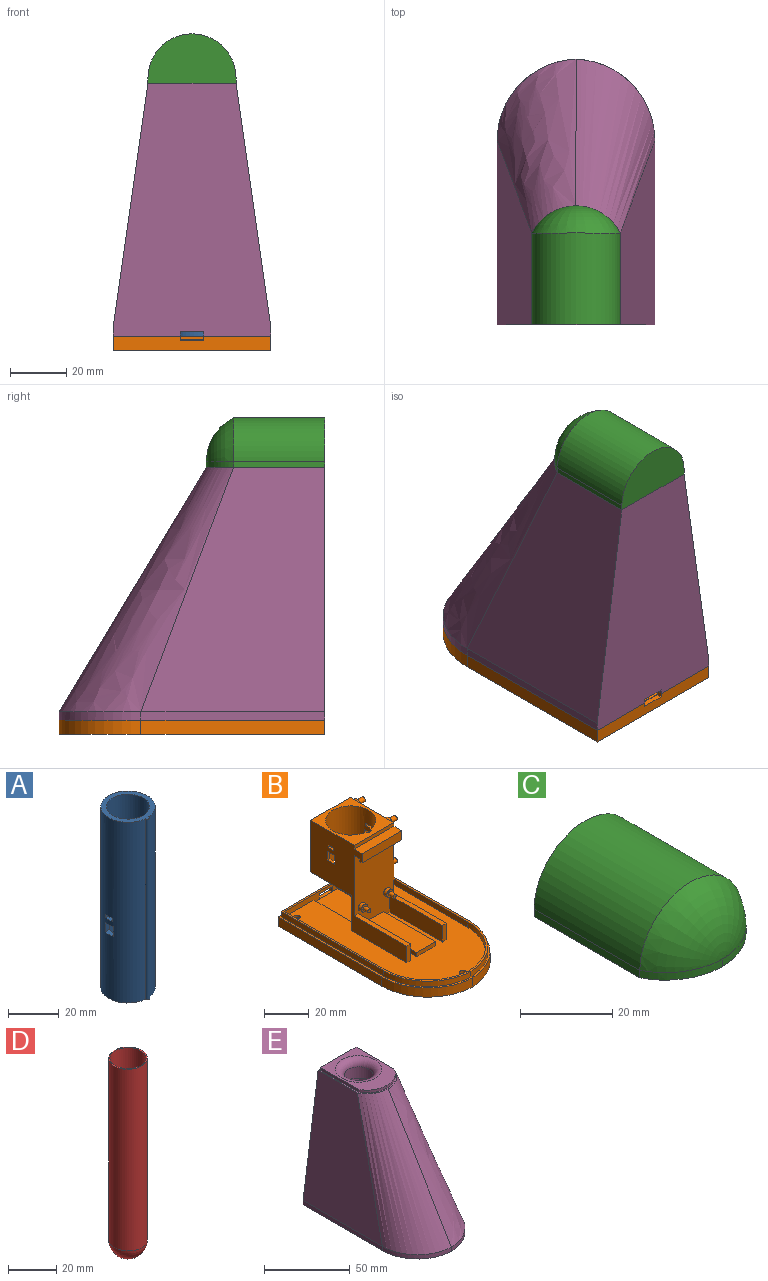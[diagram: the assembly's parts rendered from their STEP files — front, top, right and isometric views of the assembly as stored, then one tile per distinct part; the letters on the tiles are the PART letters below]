
ASSEMBLY  parts=5 mates=4
PART A: 22 faces, bbox 21.5x22.5x87.5 mm
  f0: cylinder r=8.5mm len=86.5mm, axis (0,0,1), area 4564.1mm2, adj f3,f5,f6,f7,f8,f9,f10,f11
  f1: cylinder r=10.75mm len=87.5mm, axis (0,0,1), area 5679.7mm2, adj f2,f3,f4,f6,f7,f8,f9,f10
  f2: plane 22.5x21.5mm, normal (0,0,-1), area 364.7mm2, adj f1,f4
  f3: plane 22.5x21.5mm, normal (0,0,1), area 137.7mm2, adj f0,f1,f4
  f4: cylinder r=1mm len=87.5mm, axis (0,0,1), area 283mm2, adj f1,f2,f3
  f5: plane 17x17mm, normal (0,0,1), area 227mm2, adj f0
  f6: plane 2.29x1.5mm, normal (0,-1,0), area 3.4mm2, adj f0,f1,f7,f9
  f7: plane 3.6x2.44mm, normal (0,0,1), area 8.1mm2, adj f0,f1,f6,f8
  f8: plane 2.29x1.5mm, normal (0,1,0), area 3.4mm2, adj f0,f1,f7,f9
  f9: plane 3.6x2.44mm, normal (0,0,-1), area 8.1mm2, adj f0,f1,f6,f8
  f10: plane 3.6x2.44mm, normal (0,0,-1), area 8.1mm2, adj f0,f1,f11,f13
  f11: plane 2.29x1.5mm, normal (0,1,0), area 3.4mm2, adj f0,f1,f10,f12
  f12: plane 3.6x2.44mm, normal (0,0,1), area 8.1mm2, adj f0,f1,f11,f13
  f13: plane 2.29x1.5mm, normal (0,-1,0), area 3.4mm2, adj f0,f1,f10,f12
  f14: plane 4.8x2.32mm, normal (0,1,0), area 11.1mm2, adj f0,f1,f15,f17
  f15: plane 4.6x2.57mm, normal (0,0,-1), area 10.5mm2, adj f0,f1,f14,f16
  f16: plane 4.8x2.32mm, normal (0,-1,0), area 11.1mm2, adj f0,f1,f15,f17
  f17: plane 4.6x2.57mm, normal (0,0,1), area 10.5mm2, adj f0,f1,f14,f16
  f18: plane 4.6x2.57mm, normal (0,0,1), area 10.5mm2, adj f0,f1,f19,f21
  f19: plane 4.8x2.32mm, normal (0,-1,0), area 11.1mm2, adj f0,f1,f18,f20
  f20: plane 4.6x2.57mm, normal (0,0,-1), area 10.5mm2, adj f0,f1,f19,f21
  f21: plane 4.8x2.32mm, normal (0,1,0), area 11.1mm2, adj f0,f1,f18,f20
PART B: 107 faces, bbox 56.2x94.6x52.5 mm
  f0: plane 52.2x4.2mm, normal (0,-1,0), area 151.6mm2, adj f76,f80,f82,f85,f98,f99,f101,f103
  f1: plane 54.2x3mm, normal (0,1,0), area 149.5mm2, adj f2,f79,f81,f85,f103,f104,f105
  f2: plane 94.58x56.2mm, normal (0,0,1), area 264.9mm2, adj f1,f78,f79,f81,f84,f87,f88,f89
  f3: cylinder r=1.5mm len=3mm, axis (0,0,-1), area 14.1mm2, adj f76,f97
  f4: cylinder r=1.5mm len=3mm, axis (0,0,-1), area 14.1mm2, adj f76,f95
  f5: cylinder r=1.5mm len=3mm, axis (0,0,-1), area 14.1mm2, adj f76,f93
  f6: plane 33x2.5mm, normal (0,0,1), area 82.5mm2, adj f7,f30,f38,f71
  f7: plane 9x2.5mm, normal (0,-1,0), area 22.5mm2, adj f6,f38,f71,f76
  f8: plane 12x2.21mm, normal (0,-1,0), area 26.6mm2, adj f72,f73,f74,f76
  f9: plane 4.6x1.49mm, normal (0,0,-1), area 6.1mm2, adj f16,f18,f38,f61
  f10: plane 4.8x2.49mm, normal (0,-1,0), area 11.9mm2, adj f11,f17,f60,f61
  f11: plane 4.6x2.49mm, normal (0,0,1), area 10.7mm2, adj f10,f37,f60,f61
  f12: plane 3.6x1.4mm, normal (0,0,-1), area 4.7mm2, adj f21,f35,f38,f61
  f13: plane 1.5x1.4mm, normal (0,-1,0), area 2.1mm2, adj f20,f22,f39,f61
  f14: plane 3.6x1.4mm, normal (0,0,1), area 4.7mm2, adj f21,f35,f38,f61
  f15: plane 1.5x1.4mm, normal (0,1,0), area 2.1mm2, adj f20,f22,f39,f61
  f16: plane 4.8x1.49mm, normal (0,1,0), area 7.1mm2, adj f9,f19,f38,f61
  f17: plane 4.6x2.49mm, normal (0,0,-1), area 10.7mm2, adj f10,f37,f60,f61
  f18: plane 4.8x1.49mm, normal (0,-1,0), area 7.1mm2, adj f9,f19,f38,f61
  f19: plane 4.6x1.49mm, normal (0,0,1), area 6.1mm2, adj f16,f18,f38,f61
  f20: plane 3.6x1.4mm, normal (0,0,-1), area 4.7mm2, adj f13,f15,f39,f61
  f21: plane 1.5x1.4mm, normal (0,-1,0), area 2.1mm2, adj f12,f14,f38,f61
  f22: plane 3.6x1.4mm, normal (0,0,1), area 4.7mm2, adj f13,f15,f39,f61
  f23: plane 27.5x25mm, normal (0,0,1), area 287.7mm2, adj f24,f36,f38,f39,f61,f62
  f24: plane 25x2mm, normal (0,-1,0), area 50mm2, adj f23,f25,f38,f39
  f25: plane 25x5mm, normal (0,0,1), area 125mm2, adj f24,f26,f38,f39
  f26: plane 25x5mm, normal (0,-1,0), area 125mm2, adj f25,f27,f38,f39
  f27: plane 25x1.5mm, normal (0,0,-1), area 37.5mm2, adj f26,f28,f38,f39
  f28: plane 25x1.5mm, normal (0,1,0), area 37.5mm2, adj f27,f29,f38,f39
  f29: plane 25x3.5mm, normal (0,0,-1), area 87.5mm2, adj f28,f30,f38,f39
  f30: plane 42.04x25mm, normal (0,-1,0), area 954.3mm2, adj f6,f29,f31,f38,f39,f63,f65,f71
  f31: plane 33x2.5mm, normal (0,0,1), area 82.5mm2, adj f30,f32,f39,f75
  f32: plane 9x2.5mm, normal (0,-1,0), area 22.5mm2, adj f31,f39,f75,f76
  f33: plane 25x19.34mm, normal (0,1,0), area 483.5mm2, adj f34,f38,f39,f76
  f34: plane 25.5x25mm, normal (0,0,-1), area 237.7mm2, adj f33,f36,f38,f39,f61,f62
  f35: plane 1.5x1.4mm, normal (0,1,0), area 2.1mm2, adj f12,f14,f38,f61
  f36: plane 28.2x25mm, normal (0,1,0), area 705mm2, adj f23,f34,f38,f39
  f37: plane 4.8x2.49mm, normal (0,1,0), area 11.9mm2, adj f11,f17,f60,f61
  f38: plane 60.5x47.54mm, normal (-1,0,0), area 1103.4mm2, adj f6,f7,f9,f12,f14,f16,f18,f19
  f39: plane 60.5x47.54mm, normal (1,0,0), area 1034.5mm2, adj f13,f15,f20,f22,f23,f24,f25,f26
  f40: cylinder r=2.2mm len=4.4mm, axis (-1,0,0), area 22.1mm2, adj f39,f41
  f41: plane 4.4x4.4mm, normal (1,0,0), area 10.7mm2, adj f40,f48
  f42: cylinder r=2.2mm len=4.4mm, axis (-1,0,0), area 22.1mm2, adj f39,f43
  f43: plane 4.4x4.4mm, normal (1,0,0), area 10.7mm2, adj f42,f50
  f44: cylinder r=2.2mm len=4.4mm, axis (-1,0,0), area 22.1mm2, adj f39,f45
  f45: plane 4.4x4.4mm, normal (1,0,0), area 10.7mm2, adj f44,f52
  f46: cylinder r=2.2mm len=4.4mm, axis (-1,0,0), area 22.1mm2, adj f39,f47
  f47: plane 4.4x4.4mm, normal (1,0,0), area 10.7mm2, adj f46,f54
  f48: cylinder r=1.2mm len=4mm, axis (-1,0,0), area 30.2mm2, adj f41,f49
  f49: plane 2.4x2.4mm, normal (1,0,0), area 4.5mm2, adj f48
  f50: cylinder r=1.2mm len=4mm, axis (-1,0,0), area 30.2mm2, adj f43,f51
  f51: plane 2.4x2.4mm, normal (1,0,0), area 4.5mm2, adj f50
  f52: cylinder r=1.2mm len=4mm, axis (-1,0,0), area 30.2mm2, adj f45,f53
  f53: plane 2.4x2.4mm, normal (1,0,0), area 4.5mm2, adj f52
  f54: cylinder r=1.2mm len=4mm, axis (-1,0,0), area 30.2mm2, adj f47,f55
  f55: plane 2.4x2.4mm, normal (1,0,0), area 4.5mm2, adj f54
  f56: plane 5.4x1mm, normal (0,0,1), area 5.4mm2, adj f39,f57,f59,f60
  f57: plane 5.6x1mm, normal (0,-1,0), area 5.6mm2, adj f39,f56,f58,f60
  f58: plane 5.4x1mm, normal (0,0,-1), area 5.4mm2, adj f39,f57,f59,f60
  f59: plane 5.6x1mm, normal (0,1,0), area 5.6mm2, adj f39,f56,f58,f60
  f60: plane 5.6x5.4mm, normal (1,0,0), area 8.2mm2, adj f10,f11,f17,f37,f56,f57,f58,f59
  f61: cylinder r=11.25mm len=28.2mm, axis (0,0,1), area 1856.4mm2, adj f9,f10,f11,f12,f13,f14,f15,f16
  f62: cylinder r=1.5mm len=28.2mm, axis (0,0,1), area 109.6mm2, adj f23,f34,f61
  f63: cylinder r=2mm len=4mm, axis (0,1,0), area 25.1mm2, adj f30,f64
  f64: plane 4x4mm, normal (0,-1,0), area 9.4mm2, adj f63,f67
  f65: cylinder r=2mm len=4mm, axis (0,1,0), area 25.1mm2, adj f30,f66
  f66: plane 4x4mm, normal (0,-1,0), area 9.4mm2, adj f65,f69
  f67: cylinder r=1mm len=3mm, axis (0,1,0), area 18.8mm2, adj f64,f68
  f68: plane 2x2mm, normal (0,-1,0), area 3.1mm2, adj f67
  f69: cylinder r=1mm len=3mm, axis (0,1,0), area 18.8mm2, adj f66,f70
  f70: plane 2x2mm, normal (0,-1,0), area 3.1mm2, adj f69
  f71: plane 33x9mm, normal (1,0,0), area 297mm2, adj f6,f7,f30,f76
  f72: plane 33x2.21mm, normal (-1,0,0), area 73mm2, adj f8,f30,f73,f76
  f73: plane 33x12mm, normal (0,0,1), area 396mm2, adj f8,f30,f72,f74
  f74: plane 33x2.21mm, normal (1,0,0), area 73mm2, adj f8,f30,f73,f76
  f75: plane 33x9mm, normal (-1,0,0), area 297mm2, adj f30,f31,f32,f76
  f76: plane 90.58x52.2mm, normal (0,0,1), area 3423.5mm2, adj f0,f3,f4,f5,f7,f8,f30,f32
  f77: cylinder r=27.1mm len=27.08mm, axis (0,0,1), area 124.7mm2, adj f76,f80,f83,f85
  f78: cylinder r=28.1mm len=28.08mm, axis (0,0,1), area 129.4mm2, adj f2,f79,f84,f85
  f79: plane 64.5x3mm, normal (1,0,0), area 193.5mm2, adj f1,f2,f78,f85
  f80: plane 63.5x3mm, normal (-1,0,0), area 190.5mm2, adj f0,f76,f77,f85
  f81: plane 64.5x3mm, normal (-1,0,0), area 193.5mm2, adj f1,f2,f84,f85
  f82: plane 63.5x3mm, normal (1,0,0), area 190.5mm2, adj f0,f76,f83,f85
  f83: cylinder r=27.1mm len=27.08mm, axis (0,0,1), area 124.7mm2, adj f76,f77,f82,f85
  f84: cylinder r=28.1mm len=28.08mm, axis (0,0,1), area 129.4mm2, adj f2,f78,f81,f85
  f85: plane 92.58x54.2mm, normal (0,0,1), area 265.9mm2, adj f0,f1,f77,f78,f79,f80,f81,f82
  f86: plane 94.58x56.2mm, normal (0,0,-1), area 4880.1mm2, adj f87,f88,f89,f90,f91,f92,f94,f96
  f87: plane 65.5x5mm, normal (1,0,0), area 327.5mm2, adj f2,f86,f88,f91
  f88: cylinder r=29.1mm len=29.08mm, axis (0,0,1), area 223.6mm2, adj f2,f86,f87,f89
  f89: cylinder r=29.1mm len=29.08mm, axis (0,0,1), area 223.6mm2, adj f2,f86,f88,f90
  f90: plane 65.5x5mm, normal (-1,0,0), area 327.5mm2, adj f2,f86,f89,f91
  f91: plane 56.2x5mm, normal (0,1,0), area 269.5mm2, adj f2,f86,f87,f90,f103,f105,f106
  f92: cylinder r=2.8mm len=5.6mm, axis (0,0,-1), area 61.6mm2, adj f86,f93
  f93: plane 5.6x5.6mm, normal (0,0,-1), area 17.6mm2, adj f5,f92
  f94: cylinder r=2.75mm len=5.5mm, axis (0,0,-1), area 60.5mm2, adj f86,f95
  f95: plane 5.5x5.5mm, normal (0,0,-1), area 16.7mm2, adj f4,f94
  f96: cylinder r=2.8mm len=5.6mm, axis (0,0,-1), area 61.6mm2, adj f86,f97
  f97: plane 5.6x5.6mm, normal (0,0,-1), area 17.6mm2, adj f3,f96
  f98: plane 23.9x1.2mm, normal (-1,0,0), area 28.7mm2, adj f0,f76,f100,f101
  f99: plane 23.9x1.2mm, normal (1,0,0), area 28.7mm2, adj f0,f76,f100,f101
  f100: plane 15x1.2mm, normal (0,1,0), area 18mm2, adj f76,f98,f99,f101
  f101: plane 23.9x15mm, normal (0,0,1), area 358.5mm2, adj f0,f98,f99,f100,f102
  f102: plane 8.2x0.2mm, normal (0,1,0), area 1.6mm2, adj f101,f103,f105,f106
  f103: plane 3x2mm, normal (-1,0,0), area 4.4mm2, adj f0,f1,f2,f91,f102,f104,f106
  f104: plane 8.2x1mm, normal (0,0,-1), area 8.2mm2, adj f0,f1,f103,f105
  f105: plane 3x2mm, normal (1,0,0), area 4.4mm2, adj f0,f1,f2,f91,f102,f104,f106
  f106: plane 8.2x2mm, normal (0,0,1), area 16.4mm2, adj f91,f102,f103,f105
PART C: 17 faces, bbox 31.4x42.2x17.7 mm
  f0: plane 40.18x29.36mm, normal (0,0,-1), area 124.4mm2, adj f5,f6,f7,f8,f9,f14,f15,f16
  f1: extruded ~15.68x9.68mm, area 38.8mm2, adj f2,f10,f11,f12
  f2: plane 32.5x2mm, normal (1,0,0), area 65mm2, adj f1,f3,f11,f13
  f3: plane 31.36x17.68mm, normal (0,1,0), area 448.9mm2, adj f2,f4,f11,f13
  f4: plane 32.5x2mm, normal (-1,0,0), area 65mm2, adj f3,f10,f11,f13
  f5: plane 29.36x2mm, normal (0,-1,0), area 58.7mm2, adj f0,f6,f9,f11
  f6: plane 31.26x2mm, normal (-1,0,0), area 62.5mm2, adj f0,f5,f7,f11
  f7: extruded ~14.68x8.92mm, area 36.1mm2, adj f0,f6,f8,f11
  f8: extruded ~14.68x8.92mm, area 36.1mm2, adj f0,f7,f9,f11
  f9: plane 31.26x2mm, normal (1,0,0), area 62.5mm2, adj f0,f5,f8,f11
  f10: extruded ~15.68x9.68mm, area 38.8mm2, adj f1,f4,f11,f12
  f11: plane 42.18x31.36mm, normal (0,0,-1), area 131.6mm2, adj f1,f2,f3,f4,f5,f6,f7,f8
  f12: revolved ~31.36x15.68mm, area 533.4mm2, adj f1,f10,f13
  f13: cylinder r=15.68mm len=32.5mm, axis (0,1,0), area 1601mm2, adj f2,f3,f4,f12
  f14: plane 27.36x13.68mm, normal (0,-1,0), area 294mm2, adj f0,f16
  f15: revolved ~27.36x13.68mm, area 398.8mm2, adj f0,f16
  f16: cylinder r=13.68mm len=30.01mm, axis (0,1,0), area 1289.8mm2, adj f0,f14,f15
PART D: 5 faces, bbox 16x16x100 mm
  f0: sphere r=8mm, area 402.1mm2, adj f4
  f1: sphere r=7.5mm, area 353.4mm2, adj f2
  f2: cylinder r=7.5mm len=92mm, axis (0,0,-1), area 4335.4mm2, adj f1,f3
  f3: plane 16x16mm, normal (0,0,1), area 24.3mm2, adj f2,f4
  f4: cylinder r=8mm len=92mm, axis (0,0,-1), area 4624.4mm2, adj f0,f3
PART E: 58 faces, bbox 61.2x99.6x97 mm
  f0: plane 23.5x22.5mm, normal (0,0,-1), area 172.8mm2, adj f52,f53,f56
  f1: plane 90x56.2mm, normal (0,1,0), area 3964.4mm2, adj f9,f10,f15,f18,f19,f22,f49,f50
  f2: plane 54.2x3mm, normal (0,-1,0), area 149.5mm2, adj f6,f10,f11,f14,f49,f50,f51
  f3: plane 7.1x7.1mm, normal (0,0,-1), area 33.8mm2, adj f4,f38,f45,f46
  f4: cylinder r=8.16mm len=15mm, axis (0,0,-1), area 163.4mm2, adj f3,f6,f7,f26,f37,f45,f46
  f5: plane 25.74x12.8mm, normal (0,0,-1), area 224.8mm2, adj f39,f40,f43,f44
  f6: plane 92.8x54.41mm, normal (0,0,-1), area 436.4mm2, adj f2,f4,f7,f8,f11,f12,f13,f14
  f7: plane 84.5x47.72mm, normal (0,-1,0), area 3140.6mm2, adj f4,f6,f8,f23,f26,f33,f34,f37
  f8: plane 84.61x62.98mm, normal (0.99,0,-0.14), area 3886.7mm2, adj f6,f7,f23,f24,f33,f34
  f9: plane 42.18x31.36mm, normal (0,0,1), area 131.6mm2, adj f1,f19,f20,f21,f22,f27,f28,f29
  f10: plane 94.58x56.2mm, normal (0,0,-1), area 264.9mm2, adj f1,f2,f11,f12,f13,f14,f15,f16
  f11: plane 64.5x3mm, normal (-1,0,0), area 193.5mm2, adj f2,f6,f10,f12
  f12: cylinder r=28.1mm len=28.08mm, axis (0,0,-1), area 129.4mm2, adj f6,f10,f11,f13
  f13: cylinder r=28.1mm len=28.08mm, axis (0,0,-1), area 129.4mm2, adj f6,f10,f12,f14
  f14: plane 64.5x3mm, normal (1,0,0), area 193.5mm2, adj f2,f6,f10,f13
  f15: plane 65.5x3mm, normal (-1,0,0), area 196.5mm2, adj f1,f10,f16,f19
  f16: cylinder r=29.1mm len=29.08mm, axis (0,0,-1), area 134.1mm2, adj f10,f15,f17,f20
  f17: cylinder r=29.1mm len=29.08mm, axis (0,0,-1), area 134.1mm2, adj f10,f16,f18,f21
  f18: plane 65.5x3mm, normal (1,0,0), area 196.5mm2, adj f1,f10,f17,f22
  f19: plane 87x65.5mm, normal (-0.99,0,0.14), area 4306.2mm2, adj f1,f9,f15,f20
  f20: bspline ~87x62.08mm, area 3059.1mm2, adj f9,f16,f19,f21
  f21: bspline ~87x62.08mm, area 3059.1mm2, adj f9,f17,f20,f22
  f22: plane 87x65.5mm, normal (0.99,0,0.14), area 4306.2mm2, adj f1,f9,f18,f21
  f23: plane 38.27x27.02mm, normal (0,0,-1), area 416mm2, adj f7,f8,f24,f25,f26,f54,f55
  f24: offset ~92x67.08mm, area 2409mm2, adj f6,f8,f23,f25,f39
  f25: offset ~92x67.08mm, area 2409mm2, adj f6,f23,f24,f26,f39
  f26: plane 84.61x62.98mm, normal (-0.99,0,-0.14), area 3886.7mm2, adj f4,f6,f7,f23,f25,f37
  f27: plane 31.26x2mm, normal (-1,0,0), area 62.5mm2, adj f9,f28,f30,f32
  f28: plane 29.36x2mm, normal (0,1,0), area 58.7mm2, adj f9,f27,f31,f32
  f29: bspline ~14.79x9.13mm, area 36.1mm2, adj f9,f30,f31,f32
  f30: bspline ~14.79x9.13mm, area 36.1mm2, adj f9,f27,f29,f32
  f31: plane 31.26x2mm, normal (1,0,0), area 62.5mm2, adj f9,f28,f29,f32
  f32: plane 40.18x29.37mm, normal (0,0,1), area 534.2mm2, adj f27,f28,f29,f30,f31,f52
  f33: cylinder r=8.16mm len=15mm, axis (0,0,-1), area 163.4mm2, adj f6,f7,f8,f34,f36,f47,f48
  f34: plane 7.34x5.9mm, normal (0,0,1), area 28.1mm2, adj f7,f8,f33,f35
  f35: cylinder r=1mm len=15mm, axis (0,0,-1), area 94.2mm2, adj f34,f36
  f36: plane 7.1x7.1mm, normal (0,0,-1), area 33.8mm2, adj f33,f35,f47,f48
  f37: plane 7.34x5.9mm, normal (0,0,1), area 28.1mm2, adj f4,f7,f26,f38
  f38: cylinder r=1mm len=15mm, axis (0,0,-1), area 94.2mm2, adj f3,f37
  f39: cylinder r=13.8mm len=25.86mm, axis (0,0,-1), area 545.6mm2, adj f5,f6,f24,f25,f43,f44
  f40: cylinder r=1.5mm len=10.61mm, axis (0,0,-1), area 75.6mm2, adj f5,f41,f42
  f41: offset ~92x57.68mm, area 6.9mm2, adj f40,f42
  f42: offset ~92x57.68mm, area 6.9mm2, adj f40,f41
  f43: cylinder r=26.1mm len=12.87mm, axis (0,0,-1), area 40.9mm2, adj f5,f6,f39,f44
  f44: cylinder r=26.1mm len=12.87mm, axis (0,0,-1), area 40.9mm2, adj f5,f6,f39,f43
  f45: plane 7.1x3mm, normal (1,0,0), area 21.3mm2, adj f3,f4,f6,f46
  f46: plane 7.1x3mm, normal (0,1,0), area 21.3mm2, adj f3,f4,f6,f45
  f47: plane 7.1x3mm, normal (-1,0,0), area 21.3mm2, adj f6,f33,f36,f48
  f48: plane 7.1x3mm, normal (0,1,0), area 21.3mm2, adj f6,f33,f36,f47
  f49: plane 1.6x1mm, normal (-1,0,0), area 1.6mm2, adj f1,f2,f10,f51
  f50: plane 1.6x1mm, normal (1,0,0), area 1.6mm2, adj f1,f2,f10,f51
  f51: plane 8.2x1mm, normal (0,0,-1), area 8.2mm2, adj f1,f2,f49,f50
  f52: torus R=13.47mm, axis (0,0,1), area 481.2mm2, adj f0,f32
  f53: cylinder r=1.5mm len=10mm, axis (0,0,1), area 38.9mm2, adj f0,f56,f57
  f54: cylinder r=3.5mm len=10mm, axis (0,0,1), area 61.8mm2, adj f23,f55,f57
  f55: cylinder r=13.25mm len=26.5mm, axis (0,0,1), area 778mm2, adj f23,f54,f57
  f56: cylinder r=11.25mm len=22.5mm, axis (0,0,1), area 677.9mm2, adj f0,f53,f57
  f57: plane 27.5x26.5mm, normal (0,0,-1), area 155.6mm2, adj f53,f54,f55,f56
PLACE A rot(axis=(0,0,1),180deg) t=(-238.14,-147.73,-201.73)mm
PLACE B rot(axis=(0,0,1),180deg) t=(-238.14,-147.73,-201.73)mm
PLACE C rot(axis=(0,0,1),180deg) t=(-225.64,-187.19,-214.7)mm
PLACE D rot(axis=(0,0,1),180deg) t=(-225.64,-170.44,-188.73)mm
PLACE E rot(axis=(0,0,1),180deg) t=(-225.64,-187.19,-214.7)mm
MATE slider D.f2 <-> B.f61  axis (0,0,1) through (-225.64,-170.44,-213.45)mm
MATE fastened E.f52 <-> A.f0  axis (0,0,-1) through (-225.64,-170.44,-127.2)mm
MATE slider C.f11 <-> E.f9  axis (0,0,-1) through (-225.64,-187.19,-124.7)mm
MATE slider E.f10 <-> B.f2  axis (0,0,1) through (-225.64,-93.61,-214.7)mm
